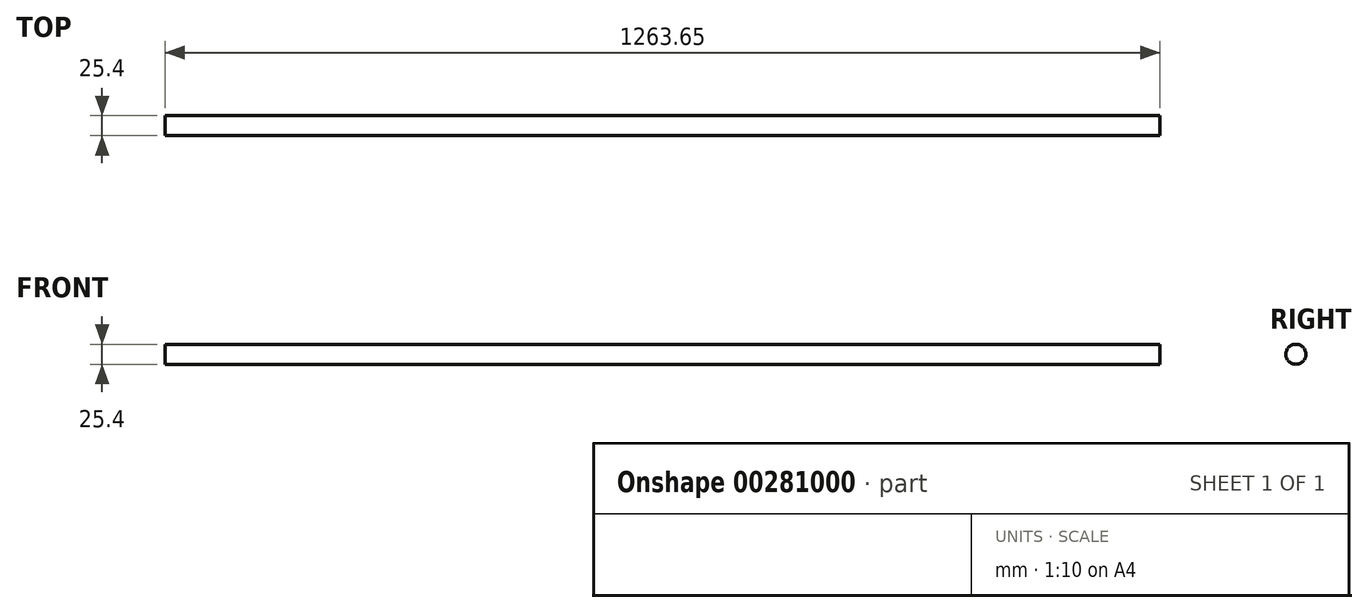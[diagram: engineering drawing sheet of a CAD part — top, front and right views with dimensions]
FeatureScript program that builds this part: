
annotation { "Feature Type Name" : "Feature", "Feature Type Description" : "" }
export const myFeature = defineFeature(function(context is Context, id is Id, definition is map)
    precondition{}
    {
        {
            var Q0;
            Q0=qCreatedBy(makeId("Top.planeOp"),FACE);
            var sketch = newSketch(context, id + "F0", { "sketchPlane" : qUnion([Q0])});
            skLineSegment(sketch, "E0", {"start": v(-650.3, 0) * mm, "end": v(613.34, 0) * mm});
            skSolve(sketch);
        }
        {
            var Q0;
            Q0=qCreatedBy(makeId("Right.planeOp"),FACE);
            var Q1;
            Q1=sQuery(id+"F0.wireOp",VERTEX,"E0.end");
            cPlane(context, id + "F1", {"entities" : qUnion([Q0, Q1]), "cplaneType" : CPlaneType.PLANE_POINT, "offset" : 25.4 * mm, "width" : 152.4 * mm, "height" : 152.4 * mm});
        }
        {
            var Q0;
            Q0=qCreatedBy(id+"F1.planeOp",FACE);
            var sketch = newSketch(context, id + "F2", { "sketchPlane" : qUnion([Q0])});
            skCircle(sketch, "E1", {"center": v(0, 0) * mm, "radius": 12.7 * mm});
            skSolve(sketch);
        }
        {
            var Q0;
            Q0=makeQuery(id+"F2.imprint","IMPRINT",FACE,{"disambiguationData":[TD([[makeQuery(id+"F2.imprint","IMPRINT",EDGE,{"derivedFrom":sQuery(id+"F2.wireOp",EDGE,"E1")}),1.0]])]});
            var Q1;
            Q1=sQuery(id+"F0.wireOp",EDGE,"E0");
            sweep(context, id + "F3", {"profiles" : qUnion([Q0]), "path" : qUnion([Q1])});
        }
    });
